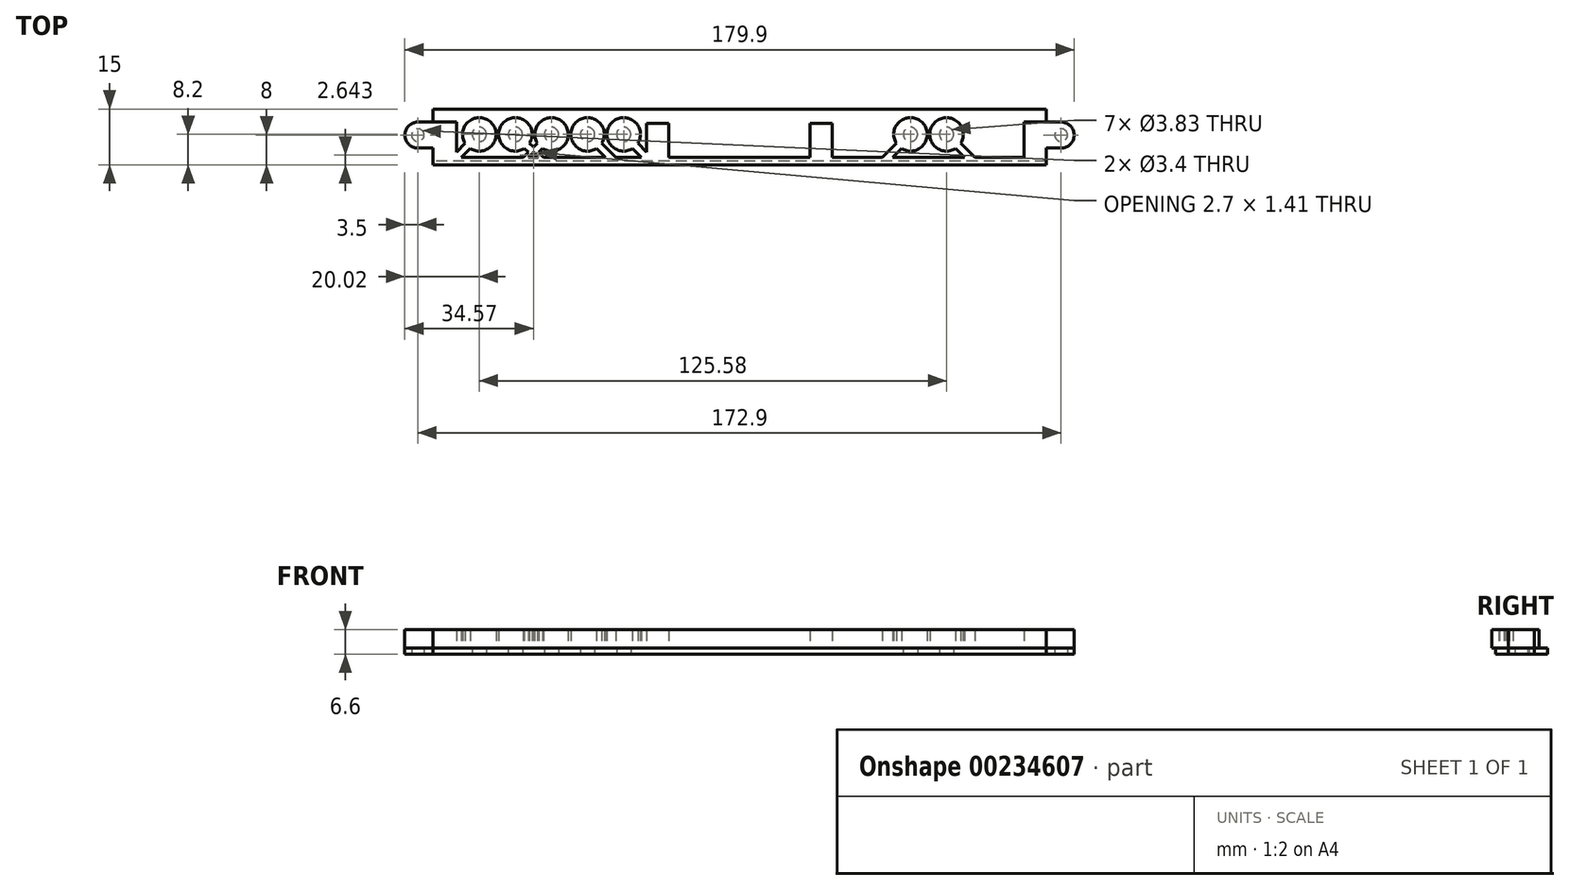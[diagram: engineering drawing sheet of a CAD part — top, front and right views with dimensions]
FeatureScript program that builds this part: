
annotation { "Feature Type Name" : "Feature", "Feature Type Description" : "" }
export const myFeature = defineFeature(function(context is Context, id is Id, definition is map)
    precondition{}
    {
        {
            var Q0;
            Q0=qCreatedBy(makeId("Top.planeOp"),FACE);
            var sketch = newSketch(context, id + "F0", { "sketchPlane" : qUnion([Q0])});
            skPoint(sketch, "E0", {"position": v(86.45, 0) * mm});
            skPoint(sketch, "E1.MirrorP", {"position": v(-86.45, 0) * mm});
            skLineSegment(sketch, "E2", {"start": v(0, -7) * mm, "end": v(82.45, -7) * mm});
            skLineSegment(sketch, "E3.MirrorCS", {"start": v(0, -7) * mm, "end": v(-82.45, -7) * mm});
            skLineSegment(sketch, "E4.MirrorCS", {"start": v(0, 7) * mm, "end": v(-82.45, 7) * mm});
            skLineSegment(sketch, "E5.MirrorCS", {"start": v(0, 7) * mm, "end": v(82.45, 7) * mm});
            skCircle(sketch, "E6", {"center": v(86.45, 0) * mm, "radius": 1.7 * mm});
            skPoint(sketch, "E7", {"position": v(-69.93, 0.2) * mm});
            skPoint(sketch, "E8", {"position": v(-4.95, 0.2) * mm});
            skPoint(sketch, "E9", {"position": v(0.85, 0.2) * mm});
            skPoint(sketch, "E10", {"position": v(55.65, 0.2) * mm});
            skPoint(sketch, "E11", {"position": v(45.95, 0.2) * mm});
            skPoint(sketch, "E12.1.0.0", {"position": v(-60.23, 0.2) * mm});
            skPoint(sketch, "E12.2.0.0", {"position": v(-50.53, 0.2) * mm});
            skPoint(sketch, "E12.3.0.0", {"position": v(-40.83, 0.2) * mm});
            skPoint(sketch, "E12.4.0.0", {"position": v(-31.13, 0.2) * mm});
            skLineSegment(sketch, "E12.direction1", {"start": v(-69.93, 0.2) * mm, "end": v(-60.23, 0.2) * mm, "construction": true});
            skCircle(sketch, "E13.MirrorC", {"center": v(-86.45, 0) * mm, "radius": 1.7 * mm});
            skLineSegment(sketch, "E14", {"start": v(82.45, -7) * mm, "end": v(82.45, -3.5) * mm});
            skLineSegment(sketch, "E15", {"start": v(82.45, 7) * mm, "end": v(82.45, 3.5) * mm});
            skLineSegment(sketch, "E16", {"start": v(82.45, 3.5) * mm, "end": v(86.45, 3.5) * mm});
            skLineSegment(sketch, "E17", {"start": v(82.45, -3.5) * mm, "end": v(86.45, -3.5) * mm});
            skArc(sketch, "E18", {"start": v(86.45, -3.5) * mm, "mid": v(89.95, 0) * mm, "end": v(86.45, 3.5) * mm});
            skLineSegment(sketch, "E19.MirrorCS", {"start": v(-82.45, 7) * mm, "end": v(-82.45, 3.5) * mm});
            skLineSegment(sketch, "E20.MirrorCS", {"start": v(-82.45, 3.5) * mm, "end": v(-86.45, 3.5) * mm});
            skArc(sketch, "E21.MirrorCS", {"start": v(-86.45, -3.5) * mm, "mid": v(-89.95, 0) * mm, "end": v(-86.45, 3.5) * mm});
            skLineSegment(sketch, "E22.MirrorCS", {"start": v(-82.45, -3.5) * mm, "end": v(-86.45, -3.5) * mm});
            skLineSegment(sketch, "E23.MirrorCS", {"start": v(-82.45, -7) * mm, "end": v(-82.45, -3.5) * mm});
            skLineSegment(sketch, "E24.bottom", {"start": v(-72.93, 3.2) * mm, "end": v(-66.93, 3.2) * mm, "construction": true});
            skLineSegment(sketch, "E24.top", {"start": v(-72.93, -2.8) * mm, "end": v(-66.93, -2.8) * mm});
            skLineSegment(sketch, "E24.left", {"start": v(-72.93, 3.2) * mm, "end": v(-72.93, -2.8) * mm, "construction": true});
            skLineSegment(sketch, "E24.right", {"start": v(-66.93, 3.2) * mm, "end": v(-66.93, -2.8) * mm, "construction": true});
            skLineSegment(sketch, "E25.1.0.0", {"start": v(-63.23, 3.2) * mm, "end": v(-57.23, 3.2) * mm, "construction": true});
            skLineSegment(sketch, "E25.1.0.1", {"start": v(-63.23, 3.2) * mm, "end": v(-63.23, -2.8) * mm, "construction": true});
            skLineSegment(sketch, "E25.1.0.2", {"start": v(-57.23, 3.2) * mm, "end": v(-57.23, -2.8) * mm, "construction": true});
            skLineSegment(sketch, "E25.1.0.4", {"start": v(-63.23, -2.8) * mm, "end": v(-57.23, -2.8) * mm, "construction": true});
            skLineSegment(sketch, "E25.2.0.0", {"start": v(-53.53, 3.2) * mm, "end": v(-47.53, 3.2) * mm, "construction": true});
            skLineSegment(sketch, "E25.2.0.1", {"start": v(-53.53, 3.2) * mm, "end": v(-53.53, -2.8) * mm, "construction": true});
            skLineSegment(sketch, "E25.2.0.2", {"start": v(-47.53, 3.2) * mm, "end": v(-47.53, -2.8) * mm, "construction": true});
            skLineSegment(sketch, "E25.2.0.4", {"start": v(-53.53, -2.8) * mm, "end": v(-47.53, -2.8) * mm, "construction": true});
            skLineSegment(sketch, "E25.3.0.0", {"start": v(-43.83, 3.2) * mm, "end": v(-37.83, 3.2) * mm, "construction": true});
            skLineSegment(sketch, "E25.3.0.1", {"start": v(-43.83, 3.2) * mm, "end": v(-43.83, -2.8) * mm, "construction": true});
            skLineSegment(sketch, "E25.3.0.2", {"start": v(-37.83, 3.2) * mm, "end": v(-37.83, -2.8) * mm, "construction": true});
            skLineSegment(sketch, "E25.3.0.4", {"start": v(-43.83, -2.8) * mm, "end": v(-37.83, -2.8) * mm, "construction": true});
            skLineSegment(sketch, "E25.4.0.0", {"start": v(-34.13, 3.2) * mm, "end": v(-28.13, 3.2) * mm, "construction": true});
            skLineSegment(sketch, "E25.4.0.1", {"start": v(-34.13, 3.2) * mm, "end": v(-34.13, -2.8) * mm, "construction": true});
            skLineSegment(sketch, "E25.4.0.2", {"start": v(-28.13, 3.2) * mm, "end": v(-28.13, -2.8) * mm, "construction": true});
            skLineSegment(sketch, "E25.4.0.4", {"start": v(-34.13, -2.8) * mm, "end": v(-28.13, -2.8) * mm, "construction": true});
            skLineSegment(sketch, "E25.direction1", {"start": v(-72.93, -2.8) * mm, "end": v(-63.23, -2.8) * mm, "construction": true});
            skLineSegment(sketch, "E26.bottom", {"start": v(42.95, 3.2) * mm, "end": v(48.95, 3.2) * mm, "construction": true});
            skLineSegment(sketch, "E26.top", {"start": v(42.95, -2.8) * mm, "end": v(48.95, -2.8) * mm, "construction": true});
            skLineSegment(sketch, "E26.left", {"start": v(42.95, 3.2) * mm, "end": v(42.95, -2.8) * mm, "construction": true});
            skLineSegment(sketch, "E26.right", {"start": v(48.95, 3.2) * mm, "end": v(48.95, -2.8) * mm, "construction": true});
            skLineSegment(sketch, "E27.1.0.1", {"start": v(52.65, -2.8) * mm, "end": v(58.65, -2.8) * mm, "construction": true});
            skLineSegment(sketch, "E27.1.0.2", {"start": v(52.65, 3.2) * mm, "end": v(52.65, -2.8) * mm, "construction": true});
            skLineSegment(sketch, "E27.1.0.3", {"start": v(58.65, 3.2) * mm, "end": v(58.65, -2.8) * mm, "construction": true});
            skLineSegment(sketch, "E27.1.0.4", {"start": v(52.65, 3.2) * mm, "end": v(58.65, 3.2) * mm, "construction": true});
            skLineSegment(sketch, "E27.direction1", {"start": v(42.95, -2.8) * mm, "end": v(52.65, -2.8) * mm, "construction": true});
            skCircle(sketch, "E28", {"center": v(-69.93, 0.2) * mm, "radius": 1.91 * mm});
            skCircle(sketch, "E29.1.0.0", {"center": v(-60.23, 0.2) * mm, "radius": 1.91 * mm});
            skCircle(sketch, "E29.2.0.0", {"center": v(-50.53, 0.2) * mm, "radius": 1.91 * mm});
            skCircle(sketch, "E29.3.0.0", {"center": v(-40.83, 0.2) * mm, "radius": 1.91 * mm});
            skCircle(sketch, "E29.4.0.0", {"center": v(-31.13, 0.2) * mm, "radius": 1.91 * mm});
            skCircle(sketch, "E30", {"center": v(45.95, 0.2) * mm, "radius": 1.91 * mm});
            skCircle(sketch, "E31", {"center": v(55.65, 0.2) * mm, "radius": 1.91 * mm});
            skSolve(sketch);
        }
        {
            var Q0;
            Q0 = qSketchRegion(id + "F0", true);
            extrude(context, id + "F1", {"entities" : qUnion([Q0]), "depth" : 1.6 * mm});
        }
        {
            var Q0;
            Q0=makeQuery(id+"F1.opExtrude","CAP_FACE",FACE,{"disambiguationData":[OSD([sQuery(id+"F0.wireOp",EDGE,"E2"),sQuery(id+"F0.wireOp",EDGE,"E3.MirrorCS"),sQuery(id+"F0.wireOp",EDGE,"E4.MirrorCS"),sQuery(id+"F0.wireOp",EDGE,"E5.MirrorCS"),sQuery(id+"F0.wireOp",EDGE,"E6"),sQuery(id+"F0.wireOp",EDGE,"E13.MirrorC"),sQuery(id+"F0.wireOp",EDGE,"E14"),sQuery(id+"F0.wireOp",EDGE,"E15"),sQuery(id+"F0.wireOp",EDGE,"E16"),sQuery(id+"F0.wireOp",EDGE,"E17"),sQuery(id+"F0.wireOp",EDGE,"E18"),sQuery(id+"F0.wireOp",EDGE,"E19.MirrorCS"),sQuery(id+"F0.wireOp",EDGE,"E20.MirrorCS"),sQuery(id+"F0.wireOp",EDGE,"E21.MirrorCS"),sQuery(id+"F0.wireOp",EDGE,"E22.MirrorCS"),sQuery(id+"F0.wireOp",EDGE,"E23.MirrorCS"),sQuery(id+"F0.wireOp",EDGE,"E24.bottom"),sQuery(id+"F0.wireOp",EDGE,"E24.top"),sQuery(id+"F0.wireOp",EDGE,"E24.left"),sQuery(id+"F0.wireOp",EDGE,"E24.right"),sQuery(id+"F0.wireOp",EDGE,"E25.1.0.0"),sQuery(id+"F0.wireOp",EDGE,"E25.1.0.1"),sQuery(id+"F0.wireOp",EDGE,"E25.1.0.2"),sQuery(id+"F0.wireOp",EDGE,"E25.1.0.4"),sQuery(id+"F0.wireOp",EDGE,"E25.2.0.0"),sQuery(id+"F0.wireOp",EDGE,"E25.2.0.1"),sQuery(id+"F0.wireOp",EDGE,"E25.2.0.2"),sQuery(id+"F0.wireOp",EDGE,"E25.2.0.4"),sQuery(id+"F0.wireOp",EDGE,"E25.3.0.0"),sQuery(id+"F0.wireOp",EDGE,"E25.3.0.1"),sQuery(id+"F0.wireOp",EDGE,"E25.3.0.2"),sQuery(id+"F0.wireOp",EDGE,"E25.3.0.4"),sQuery(id+"F0.wireOp",EDGE,"E25.4.0.0"),sQuery(id+"F0.wireOp",EDGE,"E25.4.0.1"),sQuery(id+"F0.wireOp",EDGE,"E25.4.0.2"),sQuery(id+"F0.wireOp",EDGE,"E25.4.0.4"),sQuery(id+"F0.wireOp",EDGE,"E26.bottom"),sQuery(id+"F0.wireOp",EDGE,"E26.top"),sQuery(id+"F0.wireOp",EDGE,"E26.left"),sQuery(id+"F0.wireOp",EDGE,"E26.right"),sQuery(id+"F0.wireOp",EDGE,"E27.1.0.1"),sQuery(id+"F0.wireOp",EDGE,"E27.1.0.2"),sQuery(id+"F0.wireOp",EDGE,"E27.1.0.3"),sQuery(id+"F0.wireOp",EDGE,"E27.1.0.4")])],"isStart":false});
            var sketch = newSketch(context, id + "F2", { "sketchPlane" : qUnion([Q0])});
            skLineSegment(sketch, "E32", {"start": v(-82.45, 3.5) * mm, "end": v(-86.45, 3.5) * mm});
            skLineSegment(sketch, "E33", {"start": v(-86.45, -3.5) * mm, "end": v(-82.45, -3.5) * mm});
            skLineSegment(sketch, "E34", {"start": v(-82.45, -3.5) * mm, "end": v(-82.45, -7) * mm});
            skLineSegment(sketch, "E35", {"start": v(-82.45, -7) * mm, "end": v(-82.45, -8) * mm});
            skLineSegment(sketch, "E36", {"start": v(-82.45, -8) * mm, "end": v(82.45, -8) * mm});
            skLineSegment(sketch, "E37", {"start": v(82.45, -8) * mm, "end": v(82.45, -3.5) * mm});
            skLineSegment(sketch, "E38", {"start": v(82.45, -3.5) * mm, "end": v(86.45, -3.5) * mm});
            skLineSegment(sketch, "E39", {"start": v(86.45, 3.5) * mm, "end": v(82.45, 3.5) * mm});
            skLineSegment(sketch, "E40", {"start": v(82.45, 3.5) * mm, "end": v(76.45, 3.5) * mm});
            skLineSegment(sketch, "E41", {"start": v(76.45, 3.5) * mm, "end": v(76.45, -6) * mm});
            skLineSegment(sketch, "E42", {"start": v(76.45, -6) * mm, "end": v(24.97, -6) * mm});
            skLineSegment(sketch, "E43", {"start": v(-76.1, -6) * mm, "end": v(-76.1, 3.5) * mm});
            skLineSegment(sketch, "E44", {"start": v(-76.1, 3.5) * mm, "end": v(-82.45, 3.5) * mm});
            skArc(sketch, "E45", {"start": v(-86.45, 3.5) * mm, "mid": v(-89.95, 0) * mm, "end": v(-86.45, -3.5) * mm});
            skArc(sketch, "E46", {"start": v(86.45, -3.5) * mm, "mid": v(89.95, 0) * mm, "end": v(86.45, 3.5) * mm});
            skPoint(sketch, "E47.end.orphan", {"position": v(89.95, 0) * mm});
            skPoint(sketch, "E48.firstSnap0", {"position": v(-32.97, 3.2) * mm});
            skLineSegment(sketch, "E48.bottom", {"start": v(-24.97, 3.2) * mm, "end": v(-18.97, 3.2) * mm});
            skLineSegment(sketch, "E48.left", {"start": v(-24.97, 3.2) * mm, "end": v(-24.97, -6) * mm});
            skLineSegment(sketch, "E48.right", {"start": v(-18.97, 3.2) * mm, "end": v(-18.97, -6) * mm});
            skLineSegment(sketch, "E49.MirrorCS", {"start": v(24.97, 3.2) * mm, "end": v(18.97, 3.2) * mm});
            skLineSegment(sketch, "E50.MirrorCS", {"start": v(18.97, 3.2) * mm, "end": v(18.97, -6) * mm});
            skLineSegment(sketch, "E51.MirrorCS", {"start": v(24.97, 3.2) * mm, "end": v(24.97, -6) * mm});
            skLineSegment(sketch, "E52.trimOffspring", {"start": v(18.97, -6) * mm, "end": v(-18.97, -6) * mm});
            skLineSegment(sketch, "E53.trimOffspring", {"start": v(-24.97, -6) * mm, "end": v(-76.1, -6) * mm});
            skLineSegment(sketch, "E54", {"start": v(-69.93, 0.2) * mm, "end": v(-77.13, -7) * mm});
            skLineSegment(sketch, "E55", {"start": v(-60.23, 0.2) * mm, "end": v(-53.03, -7) * mm});
            skLineSegment(sketch, "E56", {"start": v(-50.53, 0.2) * mm, "end": v(-57.73, -7) * mm});
            skLineSegment(sketch, "E57", {"start": v(-40.83, 0.2) * mm, "end": v(-33.63, -7) * mm});
            skLineSegment(sketch, "E58", {"start": v(-31.13, 0.2) * mm, "end": v(-23.93, -7) * mm});
            skArc(sketch, "E59.0.startCap", {"start": v(-70.64, 0.9) * mm, "mid": v(-69.22, 0.9) * mm, "end": v(-69.22, -0.5) * mm});
            skArc(sketch, "E59.0.endCap", {"start": v(-76.42, -7.7) * mm, "mid": v(-77.84, -7.7) * mm, "end": v(-77.84, -6.3) * mm});
            skLineSegment(sketch, "E59.0.left", {"start": v(-69.22, -0.5) * mm, "end": v(-76.42, -7.7) * mm});
            skLineSegment(sketch, "E59.0.right", {"start": v(-70.64, 0.9) * mm, "end": v(-77.84, -6.3) * mm});
            skArc(sketch, "E59.1.startCap", {"start": v(-60.94, -0.5) * mm, "mid": v(-60.94, 0.9) * mm, "end": v(-59.52, 0.9) * mm});
            skArc(sketch, "E59.1.endCap", {"start": v(-52.32, -6.3) * mm, "mid": v(-52.32, -7.7) * mm, "end": v(-53.74, -7.7) * mm});
            skLineSegment(sketch, "E59.1.left", {"start": v(-59.52, 0.9) * mm, "end": v(-52.32, -6.3) * mm});
            skLineSegment(sketch, "E59.1.right", {"start": v(-60.94, -0.5) * mm, "end": v(-53.74, -7.7) * mm});
            skArc(sketch, "E59.2.startCap", {"start": v(-51.24, 0.9) * mm, "mid": v(-49.82, 0.9) * mm, "end": v(-49.82, -0.5) * mm});
            skArc(sketch, "E59.2.endCap", {"start": v(-57.02, -7.7) * mm, "mid": v(-58.44, -7.7) * mm, "end": v(-58.44, -6.3) * mm});
            skLineSegment(sketch, "E59.2.left", {"start": v(-49.82, -0.5) * mm, "end": v(-57.02, -7.7) * mm});
            skLineSegment(sketch, "E59.2.right", {"start": v(-51.24, 0.9) * mm, "end": v(-58.44, -6.3) * mm});
            skArc(sketch, "E59.3.startCap", {"start": v(-41.54, -0.5) * mm, "mid": v(-41.54, 0.9) * mm, "end": v(-40.12, 0.9) * mm});
            skArc(sketch, "E59.3.endCap", {"start": v(-32.92, -6.3) * mm, "mid": v(-32.92, -7.7) * mm, "end": v(-34.34, -7.7) * mm});
            skLineSegment(sketch, "E59.3.left", {"start": v(-40.12, 0.9) * mm, "end": v(-32.92, -6.3) * mm});
            skLineSegment(sketch, "E59.3.right", {"start": v(-41.54, -0.5) * mm, "end": v(-34.34, -7.7) * mm});
            skArc(sketch, "E59.4.startCap", {"start": v(-31.84, -0.5) * mm, "mid": v(-31.84, 0.9) * mm, "end": v(-30.42, 0.9) * mm});
            skArc(sketch, "E59.4.endCap", {"start": v(-23.22, -6.3) * mm, "mid": v(-23.22, -7.7) * mm, "end": v(-24.64, -7.7) * mm});
            skLineSegment(sketch, "E59.4.left", {"start": v(-30.42, 0.9) * mm, "end": v(-23.22, -6.3) * mm});
            skLineSegment(sketch, "E59.4.right", {"start": v(-31.84, -0.5) * mm, "end": v(-24.64, -7.7) * mm});
            skLineSegment(sketch, "E60", {"start": v(45.95, 0.2) * mm, "end": v(38.75, -7) * mm});
            skLineSegment(sketch, "E61", {"start": v(55.65, 0.2) * mm, "end": v(62.85, -7) * mm});
            skArc(sketch, "E62.0.startCap", {"start": v(45.24, 0.9) * mm, "mid": v(46.66, 0.9) * mm, "end": v(46.66, -0.5) * mm});
            skArc(sketch, "E62.0.endCap", {"start": v(39.46, -7.7) * mm, "mid": v(38.04, -7.7) * mm, "end": v(38.04, -6.3) * mm});
            skLineSegment(sketch, "E62.0.left", {"start": v(46.66, -0.5) * mm, "end": v(39.46, -7.7) * mm});
            skLineSegment(sketch, "E62.0.right", {"start": v(45.24, 0.9) * mm, "end": v(38.04, -6.3) * mm});
            skArc(sketch, "E62.1.startCap", {"start": v(54.94, -0.5) * mm, "mid": v(54.94, 0.9) * mm, "end": v(56.36, 0.9) * mm});
            skArc(sketch, "E62.1.endCap", {"start": v(63.56, -6.3) * mm, "mid": v(63.56, -7.7) * mm, "end": v(62.14, -7.7) * mm});
            skLineSegment(sketch, "E62.1.left", {"start": v(56.36, 0.9) * mm, "end": v(63.56, -6.3) * mm});
            skLineSegment(sketch, "E62.1.right", {"start": v(54.94, -0.5) * mm, "end": v(62.14, -7.7) * mm});
            skCircle(sketch, "E63", {"center": v(-69.93, 0.2) * mm, "radius": 4.5 * mm});
            skCircle(sketch, "E64", {"center": v(45.95, 0.2) * mm, "radius": 4.5 * mm});
            skCircle(sketch, "E65", {"center": v(55.65, 0.2) * mm, "radius": 4.5 * mm});
            skCircle(sketch, "E66.1.0.0", {"center": v(-60.23, 0.2) * mm, "radius": 4.5 * mm});
            skCircle(sketch, "E66.2.0.0", {"center": v(-50.53, 0.2) * mm, "radius": 4.5 * mm});
            skCircle(sketch, "E66.3.0.0", {"center": v(-40.83, 0.2) * mm, "radius": 4.5 * mm});
            skCircle(sketch, "E66.4.0.0", {"center": v(-31.13, 0.2) * mm, "radius": 4.5 * mm});
            skLineSegment(sketch, "E66.direction1", {"start": v(-69.93, 0.2) * mm, "end": v(-60.23, 0.2) * mm, "construction": true});
            skSolve(sketch);
        }
        {
            var Q0;
            Q0 = qSketchRegion(id + "F2", true);
            extrude(context, id + "F3", {"entities" : qUnion([Q0]), "depth" : 5 * mm});
        }
    });
